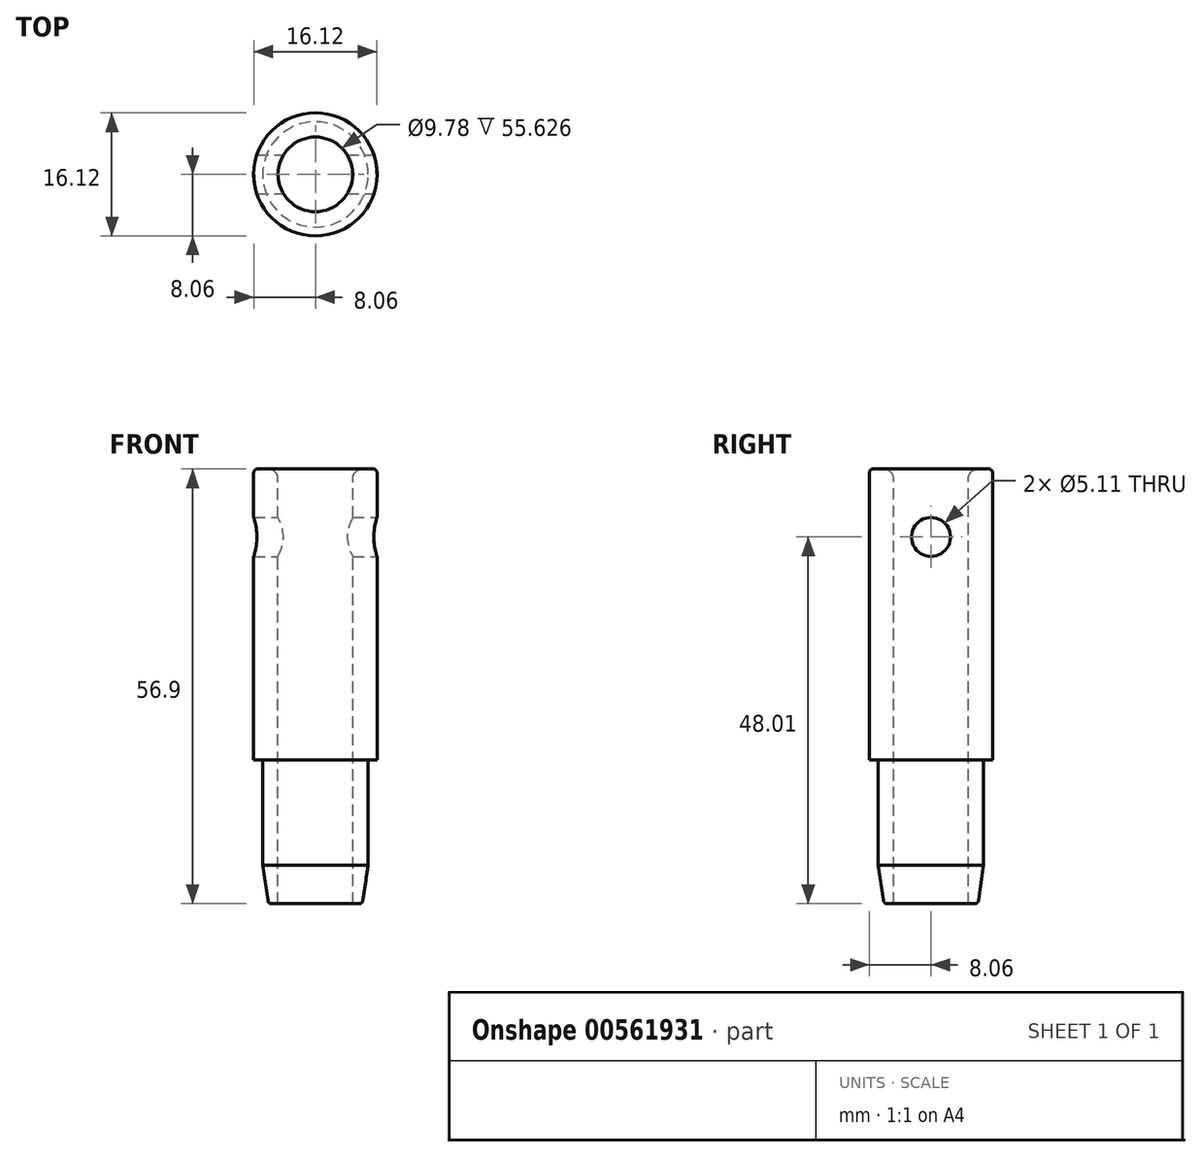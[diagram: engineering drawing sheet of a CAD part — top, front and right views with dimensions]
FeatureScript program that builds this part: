
annotation { "Feature Type Name" : "Feature", "Feature Type Description" : "" }
export const myFeature = defineFeature(function(context is Context, id is Id, definition is map)
    precondition{}
    {
        {
            var Q0;
            Q0=qCreatedBy(makeId("Front.planeOp"),FACE);
            var sketch = newSketch(context, id + "F0", { "sketchPlane" : qUnion([Q0])});
            skLineSegment(sketch, "E0", {"start": v(6.9, -3) * mm, "end": v(6.9, 10.76) * mm});
            skLineSegment(sketch, "E1", {"start": v(6.9, 10.76) * mm, "end": v(8.06, 10.76) * mm});
            skLineSegment(sketch, "E2", {"start": v(8.06, 10.76) * mm, "end": v(8.06, 48.86) * mm});
            skLineSegment(sketch, "E3", {"start": v(8.06, 48.86) * mm, "end": v(4.89, 48.86) * mm});
            skLineSegment(sketch, "E4", {"start": v(4.89, 48.86) * mm, "end": v(4.89, -8.04) * mm});
            skLineSegment(sketch, "E5", {"start": v(0, 45.5) * mm, "end": v(0, -11.02) * mm});
            skLineSegment(sketch, "E6", {"start": v(6.9, -3) * mm, "end": v(6.16, -8.04) * mm});
            skLineSegment(sketch, "E7", {"start": v(6.16, -8.04) * mm, "end": v(4.89, -8.04) * mm});
            skSolve(sketch);
        }
        {
            var Q0;
            Q0=makeQuery(id+"F0.imprint","IMPRINT",FACE,{"disambiguationData":[TD([[makeQuery(id+"F0.imprint","IMPRINT",EDGE,{"derivedFrom":sQuery(id+"F0.wireOp",EDGE,"E0")}),1.0]])]});
            var Q1;
            Q1=sQuery(id+"F0.wireOp",EDGE,"E5");
            revolve(context, id + "F1", {"entities" : qUnion([Q0]), "axis" : qUnion([Q1]), "revolveType" : RevolveType.FULL});
        }
        {
            var Q0;
            Q0=makeQuery(id+"F1.opRevolve","SWEPT_EDGE",EDGE,{"disambiguationData":[OSD([sQuery(id+"F0.wireOp",EDGE,"E3"),sQuery(id+"F0.wireOp",EDGE,"E4")])]});
            fillet(context, id + "F2", {"entities" : qUnion([Q0]), "radius" : 1.27 * mm, "tangentPropagation" : true, "allowEdgeOverflow" : false});
        }
        {
            var Q0;
            Q0=makeQuery(id+"F1.opRevolve","SWEPT_EDGE",EDGE,{"disambiguationData":[OSD([sQuery(id+"F0.wireOp",EDGE,"E2"),sQuery(id+"F0.wireOp",EDGE,"E3")])]});
            fillet(context, id + "F3", {"entities" : qUnion([Q0]), "radius" : 0.5 * mm, "tangentPropagation" : true, "allowEdgeOverflow" : false});
        }
        {
            var Q0;
            Q0=qCreatedBy(makeId("Right.planeOp"),FACE);
            var sketch = newSketch(context, id + "F4", { "sketchPlane" : qUnion([Q0])});
            skCircle(sketch, "E8", {"center": v(0, 39.97) * mm, "radius": 2.55 * mm});
            skSolve(sketch);
        }
        {
            var Q0;
            Q0=qSketchRegion(id+"F4",true);
            extrude(context, id + "F5", {"entities" : qUnion([Q0]), "operationType" : NewBodyOperationType.REMOVE, "endBound" : BoundingType.SYMMETRIC, "oppositeDirection" : true, "depth" : 25.4 * mm, "offsetDistance" : 25.4 * mm});
        }
        {
            var Q0;
            Q0=makeQuery(id+"F1.opRevolve","SWEPT_EDGE",EDGE,{"disambiguationData":[OSD([sQuery(id+"F0.wireOp",EDGE,"E6"),sQuery(id+"F0.wireOp",EDGE,"E7")])]});
            fillet(context, id + "F6", {"entities" : qUnion([Q0]), "radius" : 0.5 * mm, "tangentPropagation" : true, "allowEdgeOverflow" : false});
        }
    });
